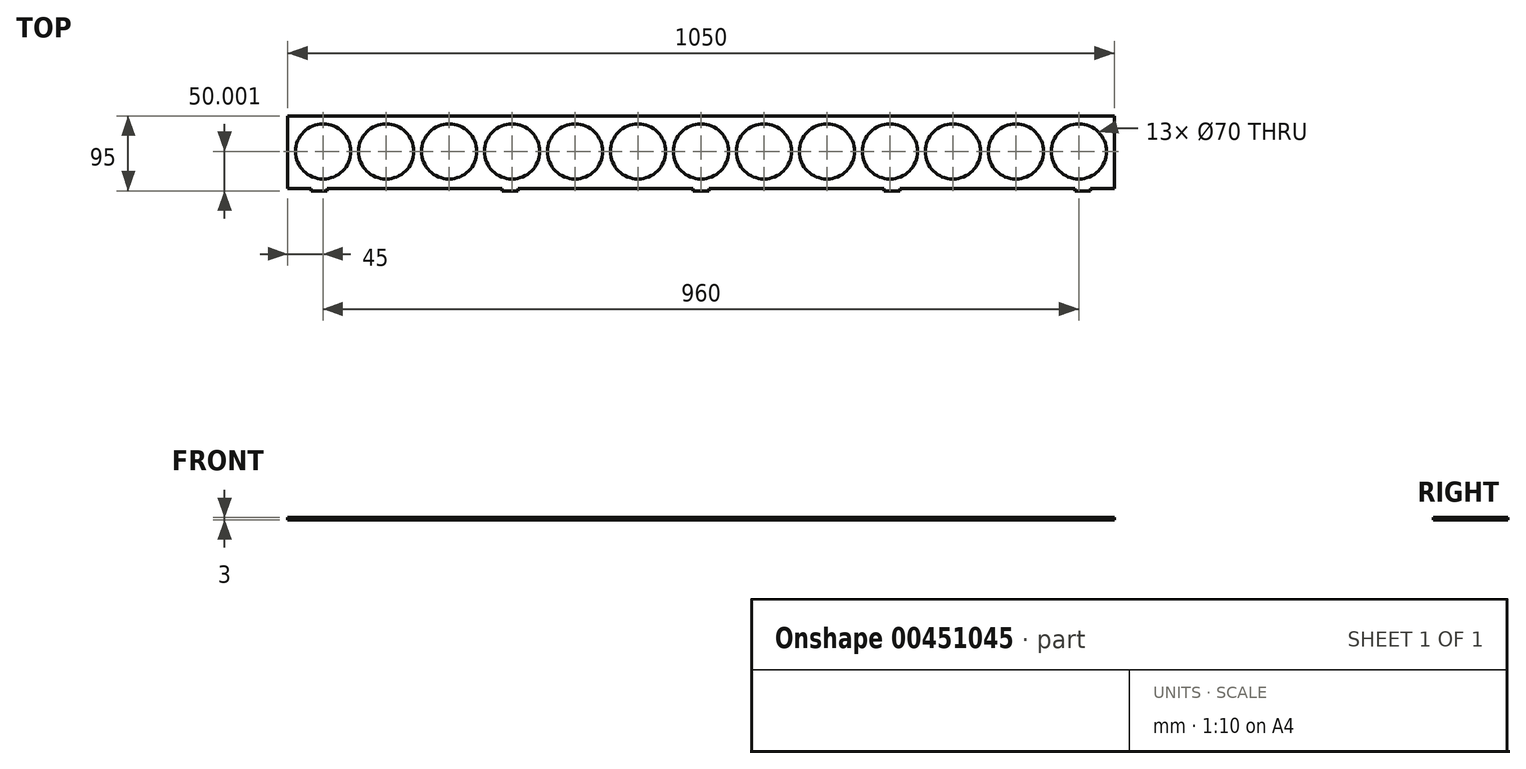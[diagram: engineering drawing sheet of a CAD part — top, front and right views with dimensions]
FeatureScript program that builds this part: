
annotation { "Feature Type Name" : "Feature", "Feature Type Description" : "" }
export const myFeature = defineFeature(function(context is Context, id is Id, definition is map)
    precondition{}
    {
        {
            var Q0;
            Q0=qCreatedBy(makeId("Top.planeOp"),FACE);
            var sketch = newSketch(context, id + "F0", { "sketchPlane" : qUnion([Q0])});
            skLineSegment(sketch, "E0.bottom", {"start": v(-525, 99.13) * mm, "end": v(525, 99.13) * mm});
            skLineSegment(sketch, "E0.left", {"start": v(-525, 99.13) * mm, "end": v(-525, 7.13) * mm});
            skLineSegment(sketch, "E0.right", {"start": v(525, 99.13) * mm, "end": v(525, 7.13) * mm});
            skCircle(sketch, "E1", {"center": v(-480, 54.13) * mm, "radius": 35 * mm});
            skCircle(sketch, "E2.1.0.0", {"center": v(-400, 54.13) * mm, "radius": 35 * mm});
            skCircle(sketch, "E2.2.0.0", {"center": v(-320, 54.13) * mm, "radius": 35 * mm});
            skCircle(sketch, "E2.3.0.0", {"center": v(-240, 54.13) * mm, "radius": 35 * mm});
            skCircle(sketch, "E2.4.0.0", {"center": v(-160, 54.13) * mm, "radius": 35 * mm});
            skCircle(sketch, "E2.5.0.0", {"center": v(-80, 54.13) * mm, "radius": 35 * mm});
            skCircle(sketch, "E2.6.0.0", {"center": v(0, 54.13) * mm, "radius": 35 * mm});
            skCircle(sketch, "E2.7.0.0", {"center": v(80, 54.13) * mm, "radius": 35 * mm});
            skCircle(sketch, "E2.8.0.0", {"center": v(160, 54.13) * mm, "radius": 35 * mm});
            skLineSegment(sketch, "E2.direction1", {"start": v(-480, 54.13) * mm, "end": v(-400, 54.13) * mm, "construction": true});
            skLineSegment(sketch, "E3", {"start": v(-525, 7.13) * mm, "end": v(-495, 7.13) * mm});
            skCircle(sketch, "E4.0.9.0", {"center": v(240, 54.13) * mm, "radius": 35 * mm});
            skCircle(sketch, "E4.0.10.0", {"center": v(320, 54.13) * mm, "radius": 35 * mm});
            skCircle(sketch, "E4.0.11.0", {"center": v(400, 54.13) * mm, "radius": 35 * mm});
            skCircle(sketch, "E4.0.12.0", {"center": v(480, 54.13) * mm, "radius": 35 * mm});
            skLineSegment(sketch, "E5", {"start": v(-485, 4.13) * mm, "end": v(-495, 4.13) * mm});
            skLineSegment(sketch, "E6", {"start": v(-495, 4.13) * mm, "end": v(-495, 7.13) * mm});
            skLineSegment(sketch, "E7.MirrorCS", {"start": v(-485, 4.13) * mm, "end": v(-475, 4.13) * mm});
            skLineSegment(sketch, "E8.MirrorCS", {"start": v(-475, 4.13) * mm, "end": v(-475, 7.13) * mm});
            skLineSegment(sketch, "E9.1.0.0", {"start": v(-242.5, 4.13) * mm, "end": v(-232.5, 4.13) * mm});
            skLineSegment(sketch, "E9.1.0.1", {"start": v(-232.5, 4.13) * mm, "end": v(-232.5, 7.13) * mm});
            skLineSegment(sketch, "E9.1.0.2", {"start": v(-242.5, 4.13) * mm, "end": v(-252.5, 4.13) * mm});
            skLineSegment(sketch, "E9.1.0.3", {"start": v(-252.5, 4.13) * mm, "end": v(-252.5, 7.13) * mm});
            skLineSegment(sketch, "E9.2.0.0", {"start": v(0, 4.13) * mm, "end": v(10, 4.13) * mm});
            skLineSegment(sketch, "E9.2.0.1", {"start": v(10, 4.13) * mm, "end": v(10, 7.13) * mm});
            skLineSegment(sketch, "E9.2.0.2", {"start": v(0, 4.13) * mm, "end": v(-10, 4.13) * mm});
            skLineSegment(sketch, "E9.2.0.3", {"start": v(-10, 4.13) * mm, "end": v(-10, 7.13) * mm});
            skLineSegment(sketch, "E9.3.0.0", {"start": v(242.5, 4.13) * mm, "end": v(252.5, 4.13) * mm});
            skLineSegment(sketch, "E9.3.0.1", {"start": v(252.5, 4.13) * mm, "end": v(252.5, 7.13) * mm});
            skLineSegment(sketch, "E9.3.0.2", {"start": v(242.5, 4.13) * mm, "end": v(232.5, 4.13) * mm});
            skLineSegment(sketch, "E9.3.0.3", {"start": v(232.5, 4.13) * mm, "end": v(232.5, 7.13) * mm});
            skLineSegment(sketch, "E9.4.0.0", {"start": v(485, 4.13) * mm, "end": v(495, 4.13) * mm});
            skLineSegment(sketch, "E9.4.0.1", {"start": v(495, 4.13) * mm, "end": v(495, 7.13) * mm});
            skLineSegment(sketch, "E9.4.0.2", {"start": v(485, 4.13) * mm, "end": v(475, 4.13) * mm});
            skLineSegment(sketch, "E9.4.0.3", {"start": v(475, 4.13) * mm, "end": v(475, 7.13) * mm});
            skLineSegment(sketch, "E9.direction1", {"start": v(-485, 4.13) * mm, "end": v(-242.5, 4.13) * mm, "construction": true});
            skLineSegment(sketch, "E10.trimOffspring", {"start": v(-475, 7.13) * mm, "end": v(-252.5, 7.13) * mm});
            skLineSegment(sketch, "E11.trimOffspring", {"start": v(-232.5, 7.13) * mm, "end": v(-10, 7.13) * mm});
            skLineSegment(sketch, "E12.trimOffspring", {"start": v(10, 7.13) * mm, "end": v(232.5, 7.13) * mm});
            skLineSegment(sketch, "E13.trimOffspring", {"start": v(495, 7.13) * mm, "end": v(525, 7.13) * mm});
            skLineSegment(sketch, "E14.trimOffspring", {"start": v(252.5, 7.13) * mm, "end": v(475, 7.13) * mm});
            skSolve(sketch);
        }
        {
            var Q0;
            Q0=qSketchRegion(id+"F0",true);
            extrude(context, id + "F1", {"entities" : qUnion([Q0]), "depth" : 3 * mm});
        }
    });
